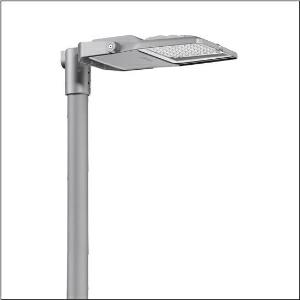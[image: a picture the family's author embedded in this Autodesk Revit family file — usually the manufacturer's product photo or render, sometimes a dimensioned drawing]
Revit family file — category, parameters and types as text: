
# Revit family: floodlight_fl_21_iq_mini___pl61_5xa7771c4c3a_1011
name_source: partatom
category: Lighting Fixtures
units: mm (PartAtom-declared; Revit-internal decimal feet)

## family parameters
Cut with Voids When Loaded = No
Host = Face
Light Source = No
Part Type = Normal
Room Calculation Point = No
Round Connector Dimension = Use Diameter
Shared = No

## types (1)
- --- (1 x LED, 12490 lm, 87.2 W, 4000K)
    Apparent Load = 87 VA
    CIE Flux Codes = 33 65 98 100 100
    Color Rendering = 70
    Color Temperature = 4000K
    Default Elevation = 1800 mm
    Description = Floodlight FL 21 iQ mini, floodlight, primary light control with lens, of PMMA, primary optical cover: protective disc, of toughened safety glass, transparent, light distribution: PL61, light emission: direct distribution, installation type: surface-mounted, LED, High Power LED, rated luminous flux: 12.490lm, luminous efficacy: 143lm/W, light colour: 740, colour temperature: 4000K, control: Auto-Match, Temp-Guard, Lumen-Switch, Night-Set, Smart-Wire, Light-Fading, Desk-Remote (wireless, voltage-free reading and setting of iQ features in the workshop via application-optimized NFC function/RFID function), optimised constant luminous flux control (CLO 2.0), with terminal, 6-pole, mains connection: 220..240V, AC, 50/60Hz, start of lifetime: 87W, end of service life: 92W, reduction: 40W, luminaire housing, of diecast aluminium, powder-coated, Siteco® metallic grey (DB 702S), corrosivity category C5 mid according to DIN EN ISO 12944, sealing non-destructively replaceable, please order mast flange separately, mast bracket, of steel, galvanised, powder-coated, Siteco® metallic grey (DB 702S), protection rating (complete): IP66, insulation class (complete): insulation class II (safety insulation), certification: CE, ENEC, VDE, protection symbol: D, impact resistance: IK08, permissible operating ambient temperature: -40..+40°C, permissible operating ambient temperature for outdoor applications: -40..+50°C, standard: DIN EN 12944, LABS conformity tested according to VDMA 24364:2018-05, packaging unit: 1 piece

Light Distribution: PL61
    Height = 70 mm
    Lamp = 1 x LED
    Lamp Light Flux = 12490 lm
    Lamp Power = 87.2 W
    Lamp count = 1
    Length = 485 mm
    Luminous efficacy = 143 lm/W
    Manufacturer = Siteco
    ModVariant = No
    Model = 5XA7771C4C3A
    Number of Poles = 1
    OnlyDefault = Yes
    Power Factor = 1
    Product Name = Floodlight FL 21 iQ mini | PL61
    Product group = floodlight | pylon annexe
    ProductGroupID = 6200
    Protection Class = Protection class II
    Protection Degree = IP 66
    RLX_Detail_Level = 1
    RLX_Emergency_Light_Flux = 0 lm
    RLX_Emergency_Type = 0
    RLX_Emergency_Type_DB = No
    RlxData = <blob elided: 101433 chars, md5=b769b021>
    Socket = socket
    Standby Power = 0 W
    System Light Flux = 12490 lm
    System Power = 87 W
    Type Comments = factory setting: luminous flux: 100 % | dim-lin: 254 | 456 mA
    Type Image = l_1007125.jpg
    URL = http://relux.com
    VarID = @adj_124115
    Voltage = 0 V
    Weight = 0.00 kg
    Width = 337 mm

## geometry (parser evidence)
native form markers: Blend x4, Sweep x11
no freeform markers — native parametric forms only
